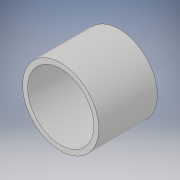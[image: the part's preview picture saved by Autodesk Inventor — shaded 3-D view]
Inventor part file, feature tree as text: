
AUTODESK INVENTOR PART (.ipt)
format: ipt  version: 2019 (Build 230136000, 136)  size: 101,376 bytes
history: native  units: mm
features: extrude x2, sketch x2
ambient origin geometry x8: Origin, YZ Plane, XZ Plane, XY Plane, X Axis, Y Axis, Z Axis, Center Point
bodies: Solid1 (feature_tree)
feature tree (4):
  extrude  "Extrusion1"  Depth=7.16mm TaperAngle=0.0deg
  extrude  "Extrusion2"  Depth=7.16mm TaperAngle=0.0deg
  sketch  "Sketch1"  dims[d0=9.32mm d1=7.16mm d2=0.0mm]
  sketch  "Sketch2"  dims[d3=8.1mm d4=7.16mm d5=0.0mm]
